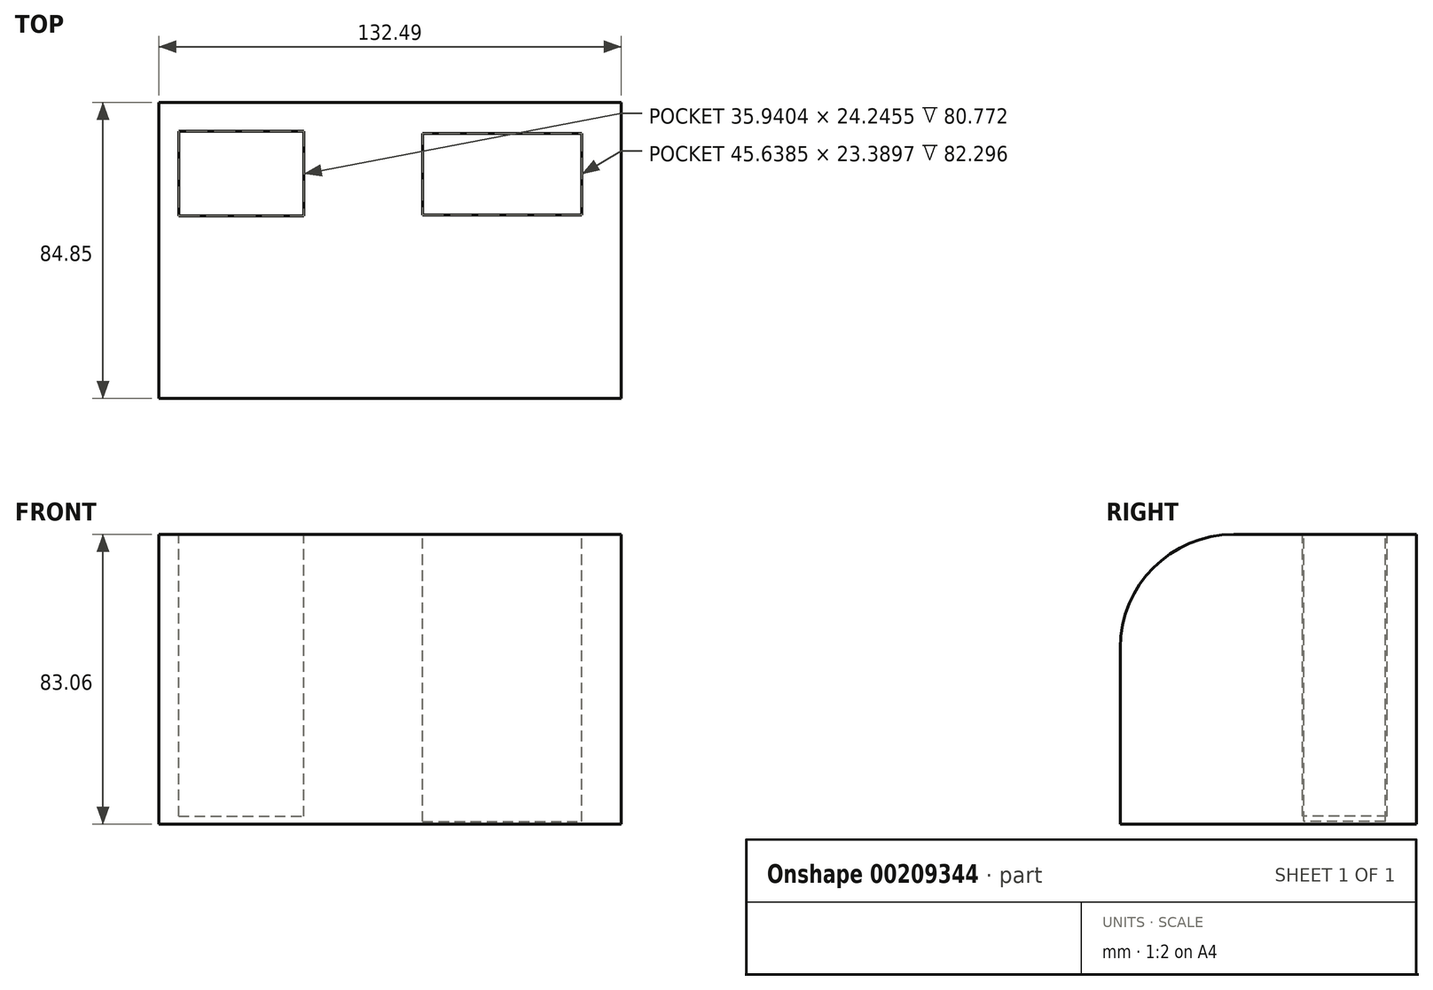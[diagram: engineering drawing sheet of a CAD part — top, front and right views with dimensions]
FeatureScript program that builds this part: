
annotation { "Feature Type Name" : "Feature", "Feature Type Description" : "" }
export const myFeature = defineFeature(function(context is Context, id is Id, definition is map)
    precondition{}
    {
        {
            var Q0;
            Q0=qCreatedBy(makeId("Top.planeOp"),FACE);
            var sketch = newSketch(context, id + "F0", { "sketchPlane" : qUnion([Q0])});
            skLineSegment(sketch, "E0.bottom", {"start": v(-63.02, 39.82) * mm, "end": v(69.47, 39.82) * mm});
            skLineSegment(sketch, "E0.top", {"start": v(-63.02, -45.03) * mm, "end": v(69.47, -45.03) * mm});
            skLineSegment(sketch, "E0.left", {"start": v(-63.02, 39.82) * mm, "end": v(-63.02, -45.03) * mm});
            skLineSegment(sketch, "E0.right", {"start": v(69.47, 39.82) * mm, "end": v(69.47, -45.03) * mm});
            skSolve(sketch);
        }
        {
            var Q0;
            Q0=makeQuery(id+"F0.imprint","IMPRINT",FACE,{"disambiguationData":[TD([[makeQuery(id+"F0.imprint","IMPRINT",EDGE,{"derivedFrom":sQuery(id+"F0.wireOp",EDGE,"E0.bottom")}),-1.0]])]});
            extrude(context, id + "F1", {"entities" : qUnion([Q0]), "depth" : 83.06 * mm});
        }
        {
            var Q0;
            Q0=makeQuery(id+"F1.opExtrude","CAP_FACE",FACE,{"disambiguationData":[OSD([sQuery(id+"F0.wireOp",EDGE,"E0.bottom"),sQuery(id+"F0.wireOp",EDGE,"E0.top"),sQuery(id+"F0.wireOp",EDGE,"E0.left"),sQuery(id+"F0.wireOp",EDGE,"E0.right")])],"isStart":false});
            var sketch = newSketch(context, id + "F2", { "sketchPlane" : qUnion([Q0])});
            skLineSegment(sketch, "E1.bottom", {"start": v(-57.33, 31.52) * mm, "end": v(-21.4, 31.52) * mm});
            skLineSegment(sketch, "E1.top", {"start": v(-57.33, 7.27) * mm, "end": v(-21.4, 7.27) * mm});
            skLineSegment(sketch, "E1.left", {"start": v(-57.33, 31.52) * mm, "end": v(-57.33, 7.27) * mm});
            skLineSegment(sketch, "E1.right", {"start": v(-21.4, 31.52) * mm, "end": v(-21.4, 7.27) * mm});
            skSolve(sketch);
        }
        {
            var Q0;
            Q0=makeQuery(id+"F2.imprint","IMPRINT",FACE,{"disambiguationData":[TD([[makeQuery(id+"F2.imprint","IMPRINT",EDGE,{"derivedFrom":sQuery(id+"F2.wireOp",EDGE,"E1.bottom")}),1.0]])]});
            var sketch = newSketch(context, id + "F3", { "sketchPlane" : qUnion([Q0])});
            skLineSegment(sketch, "E2.bottom", {"start": v(12.55, 30.95) * mm, "end": v(58.19, 30.95) * mm});
            skLineSegment(sketch, "E2.top", {"start": v(12.55, 7.56) * mm, "end": v(58.19, 7.56) * mm});
            skLineSegment(sketch, "E2.left", {"start": v(12.55, 30.95) * mm, "end": v(12.55, 7.56) * mm});
            skLineSegment(sketch, "E2.right", {"start": v(58.19, 30.95) * mm, "end": v(58.19, 7.56) * mm});
            skSolve(sketch);
        }
        {
            var Q0;
            Q0=makeQuery(id+"F2.imprint","IMPRINT",FACE,{"disambiguationData":[TD([[makeQuery(id+"F2.imprint","IMPRINT",EDGE,{"derivedFrom":sQuery(id+"F2.wireOp",EDGE,"E1.bottom")}),-1.0]])]});
            extrude(context, id + "F4", {"entities" : qUnion([Q0]), "operationType" : NewBodyOperationType.REMOVE, "oppositeDirection" : true, "depth" : 80.77 * mm});
        }
        {
            var Q0;
            Q0=makeQuery(id+"F3.imprint","IMPRINT",FACE,{"disambiguationData":[TD([[makeQuery(id+"F3.imprint","IMPRINT",EDGE,{"derivedFrom":sQuery(id+"F3.wireOp",EDGE,"E2.bottom")}),-1.0]])]});
            extrude(context, id + "F5", {"entities" : qUnion([Q0]), "operationType" : NewBodyOperationType.REMOVE, "oppositeDirection" : true, "depth" : 82.3 * mm});
        }
        {
            var Q0;
            Q0=makeQuery(id+"F1.opExtrude","CAP_EDGE",EDGE,{"disambiguationData":[OSD([sQuery(id+"F0.wireOp",EDGE,"E0.top")])],"isStart":false});
            fillet(context, id + "F6", {"entities" : qUnion([Q0]), "radius" : 32.5 * mm, "tangentPropagation" : true, "allowEdgeOverflow" : false});
        }
    });
